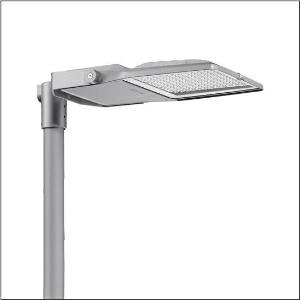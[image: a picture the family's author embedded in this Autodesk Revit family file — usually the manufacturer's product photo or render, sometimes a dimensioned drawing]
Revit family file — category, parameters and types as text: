
# Revit family: floodlight_fl_21_iq_midi___pl64_5xa7781f4e3a_1626
name_source: partatom
category: Lighting Fixtures
units: mm (PartAtom-declared; Revit-internal decimal feet)

## family parameters
Cut with Voids When Loaded = No
Host = Face
Light Source = No
Part Type = Normal
Room Calculation Point = No
Round Connector Dimension = Use Diameter
Shared = No

## types (1)
- --- (1 x LED, 36050 lm, 270.2 W, 4000K)
    Apparent Load = 270 VA
    CIE Flux Codes = 28 80 98 100 100
    Color Rendering = 70
    Color Temperature = 4000K
    Default Elevation = 1800 mm
    Description = Floodlight FL 21 iQ midi, floodlight, primary light control with lens, of PMMA, primary optical cover: protective disc, of toughened safety glass, transparent, light distribution: PL64, light emission: direct distribution, installation type: surface-mounted, LED, High Power LED, rated luminous flux: 36.050lm, luminous efficacy: 133lm/W, light colour: 740, colour temperature: 4000K, control gear: ECG iQ, control: optimised constant luminous flux control (CLO 2.0), Desk-Remote (wireless, voltage-free reading and setting of iQ features in the workshop via application-optimized NFC function/RFID function), Light-Fading, Smart-Wire, Night-Set, Lumen-Switch, Temp-Guard, Auto-Match, with terminal, 6-pole, mains connection: 220..240V, AC, 50/60Hz, start of lifetime: 270W, end of service life: 287W, reduction: 118W, luminaire housing, of diecast aluminium, powder-coated, Siteco® metallic grey (DB 702S), corrosivity category C5 mid according to DIN EN ISO 12944, sealing non-destructively replaceable, please order mast flange separately, mast bracket, of steel, galvanised, powder-coated, Siteco® metallic grey (DB 702S), protection rating (complete): IP66, insulation class (complete): insulation class II (safety insulation), certification: CE, protection symbol: D, impact resistance: IK08, permissible operating ambient temperature: -40..+40°C, permissible operating ambient temperature for outdoor applications: -40..+50°C, standard: DIN EN 12944, LABS conformity tested according to VDMA 24364:2018-05, packaging unit: 1 piece

Light Distribution: PL64
    Height = 76 mm
    Lamp = 1 x LED
    Lamp Light Flux = 36050 lm
    Lamp Power = 270.2 W
    Lamp count = 1
    Length = 657 mm
    Luminous efficacy = 133 lm/W
    Manufacturer = Siteco
    ModVariant = No
    Model = 5XA7781F4E3A
    Number of Poles = 1
    OnlyDefault = Yes
    Power Factor = 1
    Product Name = Floodlight FL 21 iQ midi | PL64
    Product group = floodlight | pylon annexe
    ProductGroupID = 6200
    Protection Class = Protection class II
    Protection Degree = IP 66
    RLX_Detail_Level = 1
    RLX_Emergency_Light_Flux = 0 lm
    RLX_Emergency_Type = 0
    RLX_Emergency_Type_DB = No
    RlxData = <blob elided: 153545 chars, md5=c11a0d05>
    Socket = socket
    Standby Power = 0 W
    System Light Flux = 36050 lm
    System Power = 270 W
    Type Comments = factory setting: luminous flux: 100 % | dim-lin: 254 | 620 mA
    Type Image = l_1007123.jpg
    URL = http://relux.com
    VarID = @adj_055077
    Voltage = 0 V
    Weight = 0.00 kg
    Width = 442 mm

## geometry (parser evidence)
native form markers: Blend x4, Sweep x13
no freeform markers — native parametric forms only
